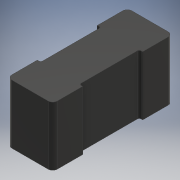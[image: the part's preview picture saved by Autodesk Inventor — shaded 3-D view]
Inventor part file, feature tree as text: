
AUTODESK INVENTOR PART (.ipt)
format: ipt  version: 2018 (Build 220112000, 112)  size: 157,696 bytes
history: native  units: mm
features: extrude x2, fillet x2, sketch x2, direct_edit x1, other x1
ambient origin geometry x8: Origin, YZ Plane, XZ Plane, XY Plane, X Axis, Y Axis, Z Axis, Center Point
bodies: Solid1 (feature_tree)
feature tree (8):
  extrude  "Extrusion1"  Depth=260.0mm
  extrude  "Extrusion2"  Depth=30.0mm
  direct_edit  "Direct Edit1"
  fillet  "Fillet2"  Radius=197.0mm
  fillet  "Fillet3"  Radius=65.0mm
  sketch  "Sketch1"  dims[d0=170.5mm d1=260.0mm]
  sketch  "Sketch2"  dims[d2=85.25mm d3=130.0mm d4=197.0mm d5=0.0mm d8=65.0mm d9=65.0mm d10=15.0mm d11=0.0mm d12=65.0mm d13=197.0mm d14=0.0mm d26=40.0mm d27=15.0mm d28=20.0mm d29=40.0mm d30=30.0mm]
  other  "Scale1"
